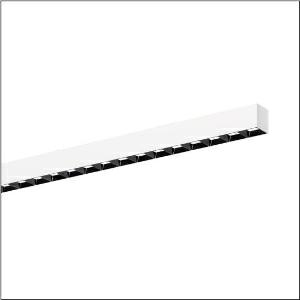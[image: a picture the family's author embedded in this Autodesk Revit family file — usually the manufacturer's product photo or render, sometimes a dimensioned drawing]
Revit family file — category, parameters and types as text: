
# Revit family: silica_r__21_51mx21da44wb_a3a2
name_source: partatom
category: Lighting Fixtures
units: mm (PartAtom-declared; Revit-internal decimal feet)

## family parameters
Cut with Voids When Loaded = No
Host = Face
Light Source = No
Part Type = Normal
Room Calculation Point = No
Round Connector Dimension = Use Diameter
Shared = No

## types (1)
- --- (1 x LED, 4320 lm, 25.6 W, 4000K)
    Apparent Load = 26 VA
    CIE Flux Codes = 87 99 100 100 100
    Color Rendering = 80
    Color Temperature = 4000K
    Default Elevation = 1800 mm
    Description = Silica® 21, office luminaire, primary light control with darklight reflector, of PMMA, black, CAT 2 (L<= 3000cd/m²), light emission: direct distribution, primary light characteristic: symmetric, installation type: surface-mounted, LED, rated luminous flux: 4.320lm, luminous efficacy: 169lm/W, light colour: 840, colour temperature: 4000K, with terminal, 3+2-pole, max. 2.5mm², mains connection: 220..240V, AC, 50/60Hz, rated input power: 25.6W, luminaire housing, of aluminium, traffic white (RAL 9016), length: 1.204mm, width: 53mm, height: 53mm, protection rating (complete): IP20, insulation class (complete): insulation class I (protective earthing), certification: CE, permissible operating ambient temperature: 0..+35°C, standard: EN 50419, packaging unit: 1 piece
    Height = 0 mm  [stored 0 ft]
    Lamp = 1 x LED
    Lamp Light Flux = 4320 lm
    Lamp Power = 25.6 W
    Lamp count = 1
    Length = 1204 mm
    Luminous efficacy = 169 lm/W
    Manufacturer = Siteco
    ModVariant = No
    Model = 51MX21DA44WB
    Mounting Place = Ceiling
    Mounting Type = Recessed
    Number of Poles = 1
    OnlyDefault = Yes
    Power Factor = 1
    Product Name = Silica® 21
    Product group = office luminaire | ceiling recessed
    ProductGroupID = 401
    Protection Class = Protection class I
    Protection Degree = IP 20
    RLX_Detail_Level = 1
    RLX_Emergency_Light_Flux = 0 lm
    RLX_Emergency_Type = 0
    RLX_Emergency_Type_DB = No
    RlxData = <blob elided: 41297 chars, md5=3ad30ff2>
    Socket = socket
    Standby Power = 0 W
    System Light Flux = 4320 lm
    System Power = 26 W
    Type Comments = factory setting: luminous flux: 100 % | dim-lin: 254 | 367 mA
    Type Image = l_1297779.jpg
    URL = http://relux.com
    VarID = @adj_054989
    Voltage = 0 V
    Weight = 0.00 kg
    Width = 53 mm

note: [stored X ft] marks values corroborated as IEEE doubles in the binary element streams (Revit-internal decimal feet)

## geometry (parser evidence)
native form markers: Blend x4, Sweep x10
no freeform markers — native parametric forms only
